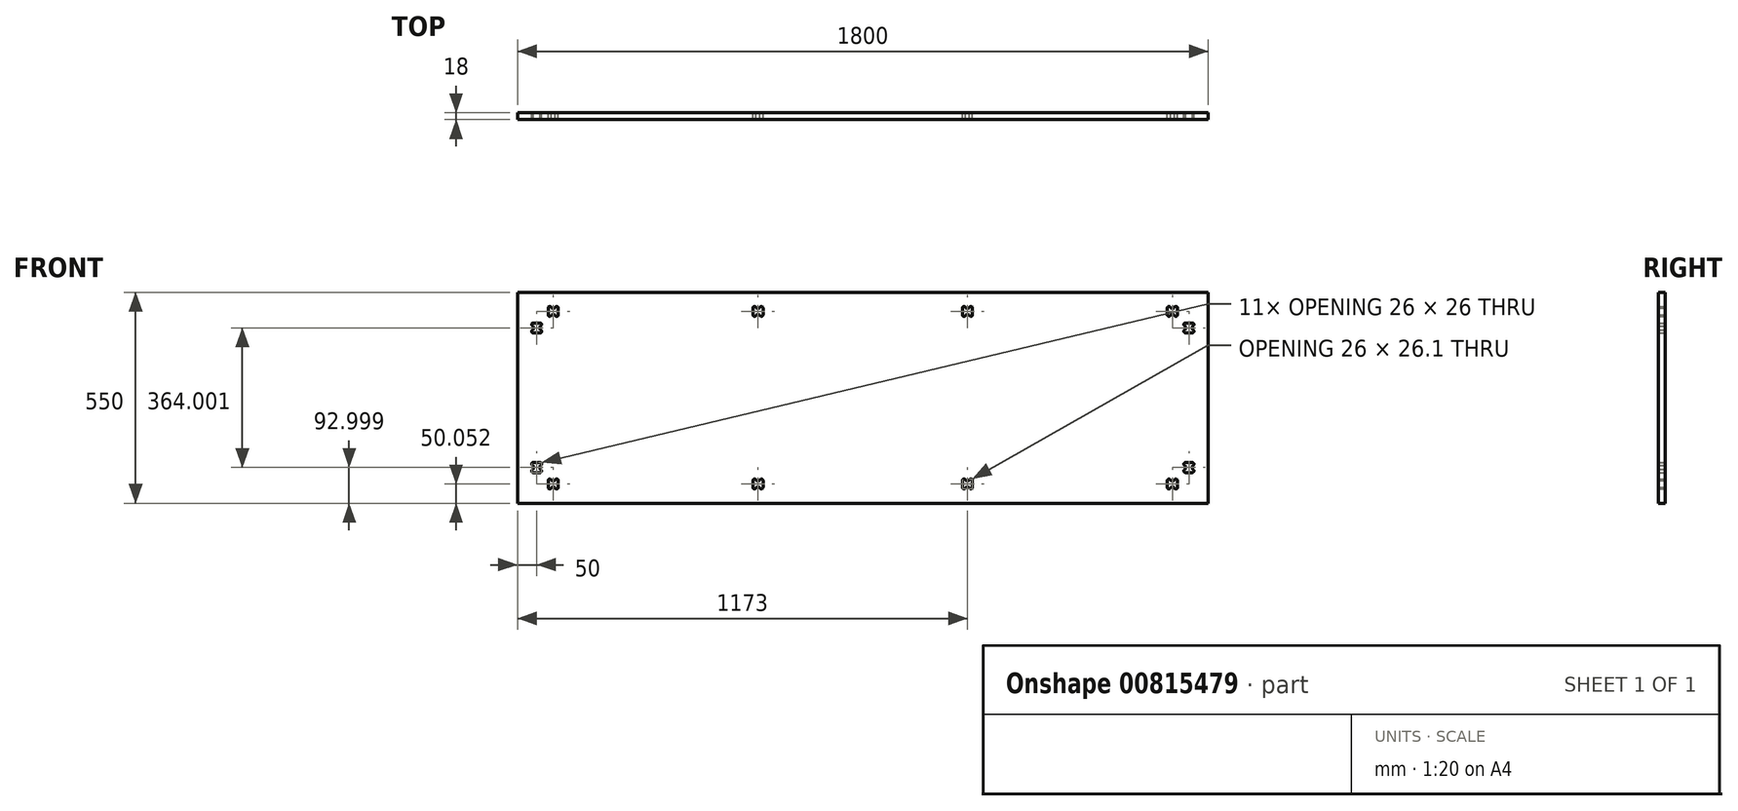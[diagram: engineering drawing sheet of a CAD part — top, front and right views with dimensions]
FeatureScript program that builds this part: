
annotation { "Feature Type Name" : "Feature", "Feature Type Description" : "" }
export const myFeature = defineFeature(function(context is Context, id is Id, definition is map)
    precondition{}
    {
        {
            var Q0;
            Q0=qCreatedBy(makeId("Front.planeOp"),FACE);
            var sketch = newSketch(context, id + "F0", { "sketchPlane" : qUnion([Q0])});
            skLineSegment(sketch, "E0.bottom", {"start": v(-900, 275) * mm, "end": v(900, 275) * mm});
            skLineSegment(sketch, "E0.top", {"start": v(-900, -275) * mm, "end": v(900, -275) * mm});
            skLineSegment(sketch, "E0.left", {"start": v(-900, 275) * mm, "end": v(-900, -275) * mm});
            skLineSegment(sketch, "E0.right", {"start": v(900, 275) * mm, "end": v(900, -275) * mm});
            skPoint(sketch, "E0.middle", {"position": v(0, 0) * mm});
            skLineSegment(sketch, "E1.bottom", {"start": v(-859, 195) * mm, "end": v(-841, 195) * mm});
            skLineSegment(sketch, "E1.top", {"start": v(-859, 169) * mm, "end": v(-841, 169) * mm});
            skLineSegment(sketch, "E1.left", {"start": v(-859, 187) * mm, "end": v(-859, 177) * mm});
            skLineSegment(sketch, "E1.right", {"start": v(-841, 187) * mm, "end": v(-841, 177) * mm});
            skArc(sketch, "E2", {"start": v(-858.9, 195) * mm, "mid": v(-863, 191.05) * mm, "end": v(-859, 187) * mm});
            skArc(sketch, "E3", {"start": v(-859, 177) * mm, "mid": v(-863, 172.95) * mm, "end": v(-858.9, 169) * mm});
            skArc(sketch, "E4", {"start": v(-841.1, 169) * mm, "mid": v(-837, 172.95) * mm, "end": v(-841, 177) * mm});
            skArc(sketch, "E5", {"start": v(-841, 187) * mm, "mid": v(-837, 191.02) * mm, "end": v(-841.04, 195) * mm});
            skPoint(sketch, "E6.start.orphan", {"position": v(-859, 182) * mm});
            skLineSegment(sketch, "E7.bottom", {"start": v(-859, -169) * mm, "end": v(-841, -169) * mm});
            skLineSegment(sketch, "E7.top", {"start": v(-859, -195) * mm, "end": v(-841, -195) * mm});
            skLineSegment(sketch, "E7.left", {"start": v(-859, -177) * mm, "end": v(-859, -187) * mm});
            skLineSegment(sketch, "E7.right", {"start": v(-841, -177) * mm, "end": v(-841, -187) * mm});
            skArc(sketch, "E8", {"start": v(-858.9, -169) * mm, "mid": v(-863, -172.95) * mm, "end": v(-859, -177) * mm});
            skArc(sketch, "E9", {"start": v(-859, -187) * mm, "mid": v(-863, -191.05) * mm, "end": v(-858.9, -195) * mm});
            skArc(sketch, "E10", {"start": v(-841.1, -195) * mm, "mid": v(-837, -191.05) * mm, "end": v(-841, -187) * mm});
            skArc(sketch, "E11", {"start": v(-841, -177) * mm, "mid": v(-837, -172.98) * mm, "end": v(-841.04, -169) * mm});
            skPoint(sketch, "E12.start.orphan", {"position": v(-859, -182) * mm});
            skLineSegment(sketch, "E13.bottom", {"start": v(-820, 216) * mm, "end": v(-820, 234) * mm});
            skLineSegment(sketch, "E13.top", {"start": v(-794, 216) * mm, "end": v(-794, 234) * mm});
            skLineSegment(sketch, "E13.left", {"start": v(-812, 216) * mm, "end": v(-802, 216) * mm});
            skLineSegment(sketch, "E13.right", {"start": v(-812, 234) * mm, "end": v(-802, 234) * mm});
            skArc(sketch, "E14", {"start": v(-820, 216.1) * mm, "mid": v(-816.05, 212) * mm, "end": v(-812, 216) * mm});
            skArc(sketch, "E15", {"start": v(-802, 216) * mm, "mid": v(-797.95, 212) * mm, "end": v(-794, 216.1) * mm});
            skArc(sketch, "E16", {"start": v(-794, 233.9) * mm, "mid": v(-797.95, 238) * mm, "end": v(-802, 234) * mm});
            skArc(sketch, "E17", {"start": v(-812, 234) * mm, "mid": v(-816.02, 238) * mm, "end": v(-820, 233.96) * mm});
            skLineSegment(sketch, "E18.bottom", {"start": v(-820, -234) * mm, "end": v(-820, -216) * mm});
            skLineSegment(sketch, "E18.top", {"start": v(-794, -234) * mm, "end": v(-794, -216) * mm});
            skLineSegment(sketch, "E18.left", {"start": v(-812, -234) * mm, "end": v(-802, -234) * mm});
            skLineSegment(sketch, "E18.right", {"start": v(-812, -216) * mm, "end": v(-802, -216) * mm});
            skArc(sketch, "E19", {"start": v(-820, -233.9) * mm, "mid": v(-816.05, -238) * mm, "end": v(-812, -234) * mm});
            skArc(sketch, "E20", {"start": v(-794, -216.1) * mm, "mid": v(-797.95, -212) * mm, "end": v(-802, -216) * mm});
            skArc(sketch, "E21", {"start": v(-812, -216) * mm, "mid": v(-816.02, -212) * mm, "end": v(-820, -216.04) * mm});
            skPoint(sketch, "E22.start.orphan", {"position": v(-850, 195) * mm});
            skLineSegment(sketch, "E23.bottom", {"start": v(794, -234) * mm, "end": v(794, -233.9) * mm});
            skLineSegment(sketch, "E23.top", {"start": v(820, -234) * mm, "end": v(820, -233.9) * mm});
            skArc(sketch, "E24", {"start": v(794, -233.9) * mm, "mid": v(797.95, -238) * mm, "end": v(802, -234) * mm});
            skArc(sketch, "E25", {"start": v(812, -234) * mm, "mid": v(816.05, -238) * mm, "end": v(820, -233.9) * mm});
            skArc(sketch, "E26", {"start": v(820, -216.1) * mm, "mid": v(816.05, -212) * mm, "end": v(812, -216) * mm});
            skArc(sketch, "E27", {"start": v(802, -216) * mm, "mid": v(797.98, -212) * mm, "end": v(794, -216.04) * mm});
            skLineSegment(sketch, "E28.trimOffspring", {"start": v(820, -216.1) * mm, "end": v(820, -216) * mm});
            skLineSegment(sketch, "E29.trimOffspring", {"start": v(794, -216.04) * mm, "end": v(794, -216) * mm});
            skLineSegment(sketch, "E30", {"start": v(794, -216) * mm, "end": v(794, -233.9) * mm});
            skLineSegment(sketch, "E31", {"start": v(802, -234) * mm, "end": v(812, -234) * mm});
            skLineSegment(sketch, "E32", {"start": v(820, -233.9) * mm, "end": v(820, -216.1) * mm});
            skLineSegment(sketch, "E33", {"start": v(802, -216) * mm, "end": v(812, -216) * mm});
            skLineSegment(sketch, "E34.bottom", {"start": v(841, -169) * mm, "end": v(859, -169) * mm});
            skLineSegment(sketch, "E34.top", {"start": v(841, -195) * mm, "end": v(859, -195) * mm});
            skLineSegment(sketch, "E34.left", {"start": v(841, -177) * mm, "end": v(841, -187) * mm});
            skLineSegment(sketch, "E34.right", {"start": v(859, -177) * mm, "end": v(859, -187) * mm});
            skArc(sketch, "E35", {"start": v(841.1, -169) * mm, "mid": v(837, -172.95) * mm, "end": v(841, -177) * mm});
            skArc(sketch, "E36", {"start": v(841, -187) * mm, "mid": v(837, -191.05) * mm, "end": v(841.1, -195) * mm});
            skArc(sketch, "E37", {"start": v(858.9, -195) * mm, "mid": v(863, -191.05) * mm, "end": v(859, -187) * mm});
            skArc(sketch, "E38", {"start": v(859, -177) * mm, "mid": v(863, -172.98) * mm, "end": v(858.96, -169) * mm});
            skLineSegment(sketch, "E39.bottom", {"start": v(841, 195) * mm, "end": v(859, 195) * mm});
            skLineSegment(sketch, "E39.top", {"start": v(841, 169) * mm, "end": v(859, 169) * mm});
            skLineSegment(sketch, "E39.left", {"start": v(841, 187) * mm, "end": v(841, 177) * mm});
            skLineSegment(sketch, "E39.right", {"start": v(859, 187) * mm, "end": v(859, 177) * mm});
            skArc(sketch, "E40", {"start": v(841.1, 195) * mm, "mid": v(837, 191.05) * mm, "end": v(841, 187) * mm});
            skArc(sketch, "E41", {"start": v(841, 177) * mm, "mid": v(837, 172.95) * mm, "end": v(841.1, 169) * mm});
            skArc(sketch, "E42", {"start": v(858.9, 169) * mm, "mid": v(863, 172.95) * mm, "end": v(859, 177) * mm});
            skArc(sketch, "E43", {"start": v(859, 187) * mm, "mid": v(863, 191.02) * mm, "end": v(858.96, 195) * mm});
            skLineSegment(sketch, "E44.bottom", {"start": v(794, 216) * mm, "end": v(794, 234) * mm});
            skLineSegment(sketch, "E44.top", {"start": v(820, 216) * mm, "end": v(820, 234) * mm});
            skLineSegment(sketch, "E44.left", {"start": v(802, 216) * mm, "end": v(812, 216) * mm});
            skLineSegment(sketch, "E44.right", {"start": v(802, 234) * mm, "end": v(812, 234) * mm});
            skArc(sketch, "E45", {"start": v(794, 216.1) * mm, "mid": v(797.95, 212) * mm, "end": v(802, 216) * mm});
            skArc(sketch, "E46", {"start": v(812, 216) * mm, "mid": v(816.05, 212) * mm, "end": v(820, 216.1) * mm});
            skArc(sketch, "E47", {"start": v(820, 233.9) * mm, "mid": v(816.05, 238) * mm, "end": v(812, 234) * mm});
            skArc(sketch, "E48", {"start": v(802, 234) * mm, "mid": v(797.98, 238) * mm, "end": v(794, 233.96) * mm});
            skLineSegment(sketch, "E49.bottom", {"start": v(-286, 216) * mm, "end": v(-286, 234) * mm});
            skLineSegment(sketch, "E49.top", {"start": v(-260, 216) * mm, "end": v(-260, 234) * mm});
            skLineSegment(sketch, "E49.left", {"start": v(-278, 216) * mm, "end": v(-268, 216) * mm});
            skLineSegment(sketch, "E49.right", {"start": v(-278, 234) * mm, "end": v(-268, 234) * mm});
            skArc(sketch, "E50", {"start": v(-286, 216.1) * mm, "mid": v(-282.05, 212) * mm, "end": v(-278, 216) * mm});
            skArc(sketch, "E51", {"start": v(-268, 216) * mm, "mid": v(-263.95, 212) * mm, "end": v(-260, 216.1) * mm});
            skArc(sketch, "E52", {"start": v(-260, 233.9) * mm, "mid": v(-263.95, 238) * mm, "end": v(-268, 234) * mm});
            skArc(sketch, "E53", {"start": v(-278, 234) * mm, "mid": v(-282.02, 238) * mm, "end": v(-286, 233.96) * mm});
            skLineSegment(sketch, "E54.bottom", {"start": v(260, 216) * mm, "end": v(260, 234) * mm});
            skLineSegment(sketch, "E54.top", {"start": v(286, 216) * mm, "end": v(286, 234) * mm});
            skLineSegment(sketch, "E54.left", {"start": v(268, 216) * mm, "end": v(278, 216) * mm});
            skLineSegment(sketch, "E54.right", {"start": v(268, 234) * mm, "end": v(278, 234) * mm});
            skArc(sketch, "E55", {"start": v(260, 216.1) * mm, "mid": v(263.95, 212) * mm, "end": v(268, 216) * mm});
            skArc(sketch, "E56", {"start": v(278, 216) * mm, "mid": v(282.05, 212) * mm, "end": v(286, 216.1) * mm});
            skArc(sketch, "E57", {"start": v(286, 233.9) * mm, "mid": v(282.05, 238) * mm, "end": v(278, 234) * mm});
            skArc(sketch, "E58", {"start": v(268, 234) * mm, "mid": v(263.98, 238) * mm, "end": v(260, 233.96) * mm});
            skLineSegment(sketch, "E59.bottom", {"start": v(-286, -234) * mm, "end": v(-286, -216) * mm});
            skLineSegment(sketch, "E59.top", {"start": v(-260, -234) * mm, "end": v(-260, -216) * mm});
            skLineSegment(sketch, "E59.left", {"start": v(-278, -234) * mm, "end": v(-268, -234) * mm});
            skLineSegment(sketch, "E59.right", {"start": v(-278, -216) * mm, "end": v(-268, -216) * mm});
            skArc(sketch, "E60", {"start": v(-286, -233.9) * mm, "mid": v(-282.05, -238) * mm, "end": v(-278, -234) * mm});
            skArc(sketch, "E61", {"start": v(-268, -234) * mm, "mid": v(-263.95, -238) * mm, "end": v(-260, -233.9) * mm});
            skArc(sketch, "E62", {"start": v(-260, -216.1) * mm, "mid": v(-263.95, -212) * mm, "end": v(-268, -216) * mm});
            skArc(sketch, "E63", {"start": v(-278, -216) * mm, "mid": v(-282.02, -212) * mm, "end": v(-286, -216.04) * mm});
            skLineSegment(sketch, "E64.bottom", {"start": v(260, -234) * mm, "end": v(260, -216) * mm});
            skLineSegment(sketch, "E64.top", {"start": v(286, -233.9) * mm, "end": v(286, -215.9) * mm});
            skLineSegment(sketch, "E64.left", {"start": v(268, -234) * mm, "end": v(278, -234) * mm});
            skLineSegment(sketch, "E64.right", {"start": v(268, -216) * mm, "end": v(278, -216) * mm});
            skArc(sketch, "E65", {"start": v(260, -233.9) * mm, "mid": v(263.95, -238) * mm, "end": v(268, -234) * mm});
            skArc(sketch, "E66", {"start": v(278, -234) * mm, "mid": v(282.1, -237.9) * mm, "end": v(286, -233.8) * mm});
            skArc(sketch, "E67", {"start": v(286, -216) * mm, "mid": v(282, -211.9) * mm, "end": v(278, -216) * mm});
            skArc(sketch, "E68", {"start": v(268, -216) * mm, "mid": v(263.98, -212) * mm, "end": v(260, -216.04) * mm});
            skPoint(sketch, "E69.end.orphan", {"position": v(-794, -234) * mm});
            skArc(sketch, "E70", {"start": v(-802, -234) * mm, "mid": v(-798, -238) * mm, "end": v(-794, -234) * mm});
            skSolve(sketch);
        }
        {
            var Q0;
            Q0=makeQuery(id+"F0.imprint","IMPRINT",FACE,{"disambiguationData":[TD([[makeQuery(id+"F0.imprint","IMPRINT",EDGE,{"derivedFrom":sQuery(id+"F0.wireOp",EDGE,"E0.bottom")}),-1.0]])]});
            extrude(context, id + "F1", {"entities" : qUnion([Q0]), "depth" : 18 * mm, "offsetDistance" : 25 * mm});
        }
    });
